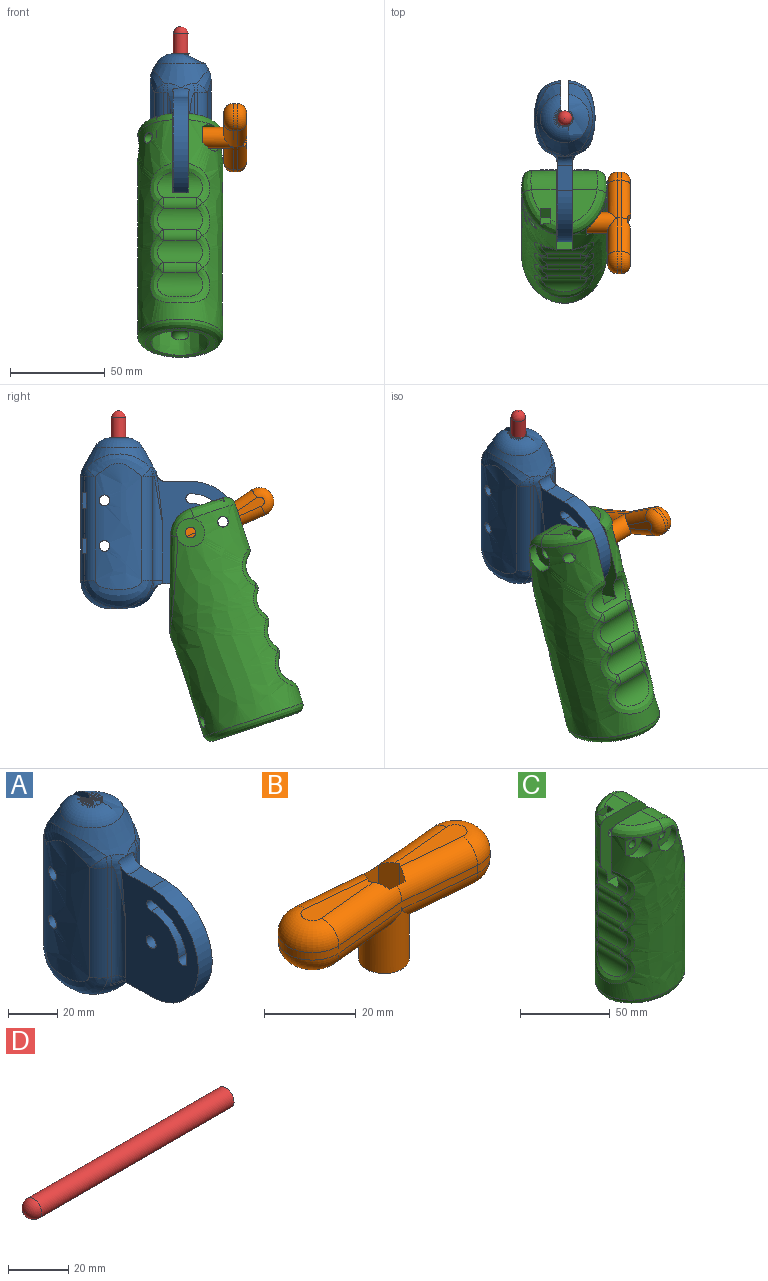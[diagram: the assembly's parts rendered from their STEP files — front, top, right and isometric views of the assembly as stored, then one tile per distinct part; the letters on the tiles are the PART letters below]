
ASSEMBLY  parts=4 mates=3
PART A: 87 faces, bbox 43.8x89x93.8 mm
  f0: cylinder r=20mm len=54.41mm, axis (0,0,-1), area 109.3mm2, adj f43,f48,f56,f66
  f1: cylinder r=20mm len=54.41mm, axis (0,0,-1), area 347.3mm2, adj f12,f14,f15,f17,f28,f29,f31,f43
  f2: torus R=10mm, axis (0,0,1), area 36.3mm2, adj f4,f13,f54,f65
  f3: torus R=10mm, axis (0,0,1), area 10mm2, adj f7,f54,f58,f74
  f4: cylinder r=20mm len=54.41mm, axis (0,0,-1), area 401.1mm2, adj f2,f13,f43,f67
  f5: plane 60.7x48.7mm, normal (1,0,0), area 1782mm2, adj f35,f36,f37,f38,f39,f40,f41,f42
  f6: plane 60.7x48.7mm, normal (-1,0,0), area 1782mm2, adj f35,f36,f37,f38,f39,f40,f41,f42
  f7: cylinder r=20mm len=54.41mm, axis (0,0,-1), area 109.3mm2, adj f3,f43,f44,f72
  f8: cylinder r=2.85mm len=5.7mm, axis (1,0,0), area 85.6mm2, adj f16,f61
  f9: cylinder r=3.95mm len=89.49mm, axis (0,0,-1), area 1833.2mm2, adj f12,f13,f26,f60,f83,f84,f85
  f10: cylinder r=2.85mm len=6mm, axis (1,0,0), area 107.4mm2, adj f13,f23
  f11: cylinder r=2.85mm len=5.7mm, axis (1,0,0), area 71.6mm2, adj f12,f17
  f12: plane 91.73x18.22mm, normal (1,0,0), area 1287.5mm2, adj f1,f9,f11,f26,f27,f43,f54,f57
  f13: plane 91.72x18.22mm, normal (-1,0,0), area 1287.5mm2, adj f2,f4,f9,f10,f25,f26,f43,f54
  f14: plane 14.05x4.5mm, normal (0,0,1), area 59mm2, adj f1,f16,f17,f19,f69
  f15: plane 14.05x4.5mm, normal (0,0,-1), area 59mm2, adj f1,f16,f17,f18,f69
  f16: plane 14.27x8.2mm, normal (1,0,0), area 81.8mm2, adj f8,f14,f15,f18,f19,f69
  f17: plane 16.41x8.2mm, normal (-1,0,0), area 99.4mm2, adj f1,f11,f14,f15,f18,f19
  f18: plane 4.5x4.1mm, normal (0,0.87,-0.5), area 21.3mm2, adj f15,f16,f17,f19
  f19: plane 4.5x4.1mm, normal (0,0.87,0.5), area 21.3mm2, adj f14,f16,f17,f18
  f20: plane 6x5.75mm, normal (0,0,-1), area 31.4mm2, adj f52,f53,f62,f79
  f21: plane 38x2.14mm, normal (0,-1,0), area 81.1mm2, adj f51,f53,f67,f82
  f22: plane 38x6mm, normal (0,1,0), area 227.8mm2, adj f50,f52,f62,f75
  f23: plane 44x12mm, normal (1,0,0), area 469.2mm2, adj f10,f25,f75,f76,f77,f78,f79,f80
  f24: cylinder r=2.85mm len=5.7mm, axis (1,0,0), area 85.6mm2, adj f30,f61
  f25: cylinder r=2.85mm len=6mm, axis (1,0,0), area 107.4mm2, adj f13,f23
  f26: plane 10x9.58mm, normal (0,0,-1), area 42.5mm2, adj f9,f12,f13,f43,f83,f84,f86
  f27: cylinder r=2.85mm len=5.7mm, axis (1,0,0), area 71.6mm2, adj f12,f31
  f28: plane 14.05x4.5mm, normal (0,0,-1), area 59mm2, adj f1,f30,f31,f33,f69
  f29: plane 14.05x4.5mm, normal (0,0,1), area 59mm2, adj f1,f30,f31,f32,f69
  f30: plane 14.27x8.2mm, normal (1,0,0), area 81.8mm2, adj f24,f28,f29,f32,f33,f69
  f31: plane 16.41x8.2mm, normal (-1,0,0), area 99.4mm2, adj f1,f27,f28,f29,f32,f33
  f32: plane 4.5x4.1mm, normal (0,0.87,0.5), area 21.3mm2, adj f29,f30,f31,f33
  f33: plane 4.5x4.1mm, normal (0,0.87,-0.5), area 21.3mm2, adj f28,f30,f31,f32
  f34: plane 6x5.75mm, normal (0,0,1), area 31.4mm2, adj f50,f51,f62,f78
  f35: plane 13.32x8mm, normal (0,0,1), area 104.9mm2, adj f5,f6,f37,f46
  f36: plane 14.6x8mm, normal (0,0,-1), area 115mm2, adj f5,f6,f37,f47
  f37: cylinder r=27mm len=54mm, axis (-1,0,0), area 678.6mm2, adj f5,f6,f35,f36
  f38: cylinder r=2.85mm len=8mm, axis (1,0,0), area 143.3mm2, adj f5,f6
  f39: cylinder r=15.5mm len=15.5mm, axis (1,0,0), area 194.8mm2, adj f5,f6,f40,f42
  f40: cylinder r=2.5mm len=8mm, axis (1,0,0), area 62.8mm2, adj f5,f6,f39,f41
  f41: cylinder r=20.5mm len=20.5mm, axis (1,0,0), area 257.6mm2, adj f5,f6,f40,f42
  f42: cylinder r=2.5mm len=8mm, axis (1,0,0), area 62.8mm2, adj f5,f6,f39,f41
  f43: torus R=5mm, axis (0,0,-1), area 773.6mm2, adj f0,f1,f4,f7,f12,f13,f26,f45
  f44: cylinder r=5mm len=54.41mm, axis (0,0,-1), area 250.9mm2, adj f6,f7,f45,f58
  f45: bspline ~10.07x6.08mm, area 23mm2, adj f6,f43,f44,f47
  f46: torus R=25mm, axis (0,0,-1), area 62.4mm2, adj f5,f6,f35,f54,f55,f58
  f47: torus R=23.73mm, axis (0,0,-1), area 62.5mm2, adj f5,f6,f36,f43,f45,f49
  f48: cylinder r=5mm len=54.41mm, axis (0,0,-1), area 250.9mm2, adj f0,f5,f49,f55
  f49: bspline ~10.07x6.08mm, area 23mm2, adj f5,f43,f47,f48
  f50: cylinder r=5mm len=6mm, axis (-1,0,0), area 46.1mm2, adj f22,f34,f62,f76
  f51: cylinder r=5mm len=5mm, axis (1,0,0), area 26.2mm2, adj f21,f34,f62,f67,f80
  f52: cylinder r=5mm len=6mm, axis (-1,0,0), area 46.1mm2, adj f20,f22,f62,f77
  f53: cylinder r=5mm len=5mm, axis (1,0,0), area 26.2mm2, adj f20,f21,f62,f67,f81
  f54: cone r=10mm half-angle=29.1deg, axis (0,0,-1), area 726.9mm2, adj f2,f3,f12,f13,f46,f55,f56,f57
  f55: bspline ~35.83x19.57mm, area 87.3mm2, adj f5,f46,f48,f54,f56
  f56: torus R=10mm, axis (0,0,1), area 10mm2, adj f0,f54,f55,f64
  f57: torus R=10mm, axis (0,0,1), area 36.3mm2, adj f1,f12,f54,f71
  f58: bspline ~35.83x19.57mm, area 87.3mm2, adj f3,f6,f44,f46,f54
  f59: torus R=4.12mm, axis (0,0,1), area 535.2mm2, adj f12,f13,f54,f60
  f60: cone r=3.95mm half-angle=46deg, axis (0,0,1), area 16mm2, adj f9,f12,f13,f59
  f61: extruded ~66.51x24.67mm, area 1528.6mm2, adj f8,f24,f69,f70,f72,f73
  f62: extruded ~66.51x24.67mm, area 960.1mm2, adj f20,f22,f34,f50,f51,f52,f53,f63
  f63: bspline ~35.46x13.76mm, area 236.7mm2, adj f54,f62,f64,f65
  f64: sphere r=10mm, area 21.4mm2, adj f56,f63,f66
  f65: sphere r=10mm, area 21.4mm2, adj f2,f63,f67
  f66: cylinder r=10mm len=54.41mm, axis (0,0,-1), area 410.2mm2, adj f0,f62,f64,f68
  f67: cylinder r=10mm len=54.41mm, axis (0,0,-1), area 251.4mm2, adj f4,f21,f51,f53,f62,f65,f68
  f68: bspline ~35.69x17.25mm, area 434mm2, adj f43,f62,f66,f67
  f69: cylinder r=10mm len=54.41mm, axis (0,0,-1), area 381.9mm2, adj f1,f14,f15,f16,f28,f29,f30,f61
  f70: bspline ~35.69x17.25mm, area 434mm2, adj f43,f61,f69,f72
  f71: sphere r=10mm, area 21.4mm2, adj f57,f69,f73
  f72: cylinder r=10mm len=54.41mm, axis (0,0,-1), area 410.2mm2, adj f7,f61,f70,f74
  f73: bspline ~36.64x13.76mm, area 236.7mm2, adj f54,f61,f71,f74
  f74: sphere r=10mm, area 21.4mm2, adj f3,f72,f73
  f75: cylinder r=2mm len=38mm, axis (0,0,-1), area 119.4mm2, adj f22,f23,f76,f77
  f76: torus R=3mm, axis (-1,0,0), area 21.1mm2, adj f23,f50,f75,f78
  f77: torus R=3mm, axis (-1,0,0), area 21.1mm2, adj f23,f52,f75,f79
  f78: cylinder r=2mm len=6mm, axis (0,-1,0), area 18.8mm2, adj f23,f34,f76,f80
  f79: cylinder r=2mm len=6mm, axis (0,-1,0), area 18.8mm2, adj f20,f23,f77,f81
  f80: torus R=3mm, axis (-1,0,0), area 21.1mm2, adj f23,f51,f78,f82
  f81: torus R=3mm, axis (-1,0,0), area 21.1mm2, adj f23,f53,f79,f82
  f82: cylinder r=2mm len=38mm, axis (0,0,1), area 119.4mm2, adj f21,f23,f80,f81
  f83: plane 3x2.41mm, normal (1,0,0), area 7.2mm2, adj f9,f26,f85,f86
  f84: plane 3x2.41mm, normal (-1,0,0), area 7.2mm2, adj f9,f26,f85,f86
  f85: plane 4.95x4mm, normal (0,0,1), area 17.4mm2, adj f9,f83,f84,f86
  f86: cylinder r=2mm len=4mm, axis (0,0,-1), area 18.8mm2, adj f26,f83,f84,f85
PART B: 32 faces, bbox 59.1x15.1x23.1 mm
  f0: plane 20.27x5mm, normal (0,0,1), area 69.4mm2, adj f4,f6,f21,f25,f26
  f1: cylinder r=2.75mm len=15mm, axis (0,0,-1), area 259.2mm2, adj f8,f31
  f2: plane 20.27x5mm, normal (0,0,1), area 69.4mm2, adj f3,f5,f20,f28,f29
  f3: cylinder r=5mm len=21.9mm, axis (1,0.09,0), area 156.8mm2, adj f2,f4,f15,f20,f29,f30
  f4: cylinder r=5mm len=21.9mm, axis (1,-0.09,0), area 156.8mm2, adj f0,f3,f16,f21,f25,f30
  f5: cylinder r=5mm len=21.9mm, axis (-1,0.09,0), area 156.8mm2, adj f2,f6,f13,f20,f27,f28
  f6: cylinder r=5mm len=21.9mm, axis (-1,-0.09,0), area 156.8mm2, adj f0,f5,f12,f21,f26,f27
  f7: cylinder r=5.5mm len=16mm, axis (0,0,-1), area 431.4mm2, adj f8,f9,f10,f17,f19,f22,f24
  f8: plane 11x11mm, normal (0,0,-1), area 71.3mm2, adj f1,f7
  f9: plane 19.09x5mm, normal (0,0,-1), area 67.6mm2, adj f7,f17,f18,f19
  f10: plane 19.09x5mm, normal (0,0,-1), area 67.6mm2, adj f7,f22,f23,f24
  f11: cylinder r=7.5mm len=15mm, axis (0,0,-1), area 49.9mm2, adj f12,f16,f18,f21
  f12: plane 21.31x2mm, normal (0.09,-1,0), area 42.8mm2, adj f6,f11,f13,f19
  f13: plane 21.31x2mm, normal (-0.09,-1,0), area 42.8mm2, adj f5,f12,f14,f24
  f14: cylinder r=7.5mm len=15mm, axis (0,0,-1), area 49.9mm2, adj f13,f15,f20,f23
  f15: plane 21.31x2mm, normal (-0.09,1,0), area 42.8mm2, adj f3,f14,f16,f22
  f16: plane 21.31x2mm, normal (0.09,1,0), area 42.8mm2, adj f4,f11,f15,f17
  f17: cylinder r=5mm len=21.77mm, axis (-1,0.09,0), area 144.9mm2, adj f7,f9,f16,f18
  f18: torus R=2.5mm, axis (0,0,1), area 148.4mm2, adj f9,f11,f17,f19
  f19: cylinder r=5mm len=21.77mm, axis (1,0.09,0), area 144.9mm2, adj f7,f9,f12,f18
  f20: torus R=2.5mm, axis (0,0,1), area 148.4mm2, adj f2,f3,f5,f14
  f21: torus R=2.5mm, axis (0,0,1), area 148.4mm2, adj f0,f4,f6,f11
  f22: cylinder r=5mm len=21.77mm, axis (-1,-0.09,0), area 144.9mm2, adj f7,f10,f15,f23
  f23: torus R=2.5mm, axis (0,0,1), area 148.4mm2, adj f10,f14,f22,f24
  f24: cylinder r=5mm len=21.77mm, axis (1,-0.09,0), area 144.9mm2, adj f7,f10,f13,f23
  f25: plane 8.12x4.22mm, normal (0.87,-0.5,0), area 36.3mm2, adj f0,f4,f26,f30,f31
  f26: plane 8.12x4.22mm, normal (0.87,0.5,0), area 36.3mm2, adj f0,f6,f25,f27,f31
  f27: plane 6.71x4.77mm, normal (0,1,0), area 31.1mm2, adj f5,f6,f26,f28,f31
  f28: plane 8.12x4.22mm, normal (-0.87,0.5,0), area 36.3mm2, adj f2,f5,f27,f29,f31
  f29: plane 8.12x4.22mm, normal (-0.87,-0.5,0), area 36.3mm2, adj f2,f3,f28,f30,f31
  f30: plane 6.71x4.77mm, normal (0,-1,0), area 31.1mm2, adj f3,f4,f25,f29,f31
  f31: plane 9.47x8.2mm, normal (0,0,1), area 34.5mm2, adj f1,f25,f26,f27,f28,f29,f30
PART C: 55 faces, bbox 56x46x120.9 mm
  f0: plane 47.01x37.01mm, normal (0,0,-1), area 368.9mm2, adj f23,f33
  f1: cylinder r=2.8mm len=7.8mm, axis (0,-1,0), area 137.2mm2, adj f9,f22
  f2: extruded ~111x54.98mm, area 11755.2mm2, adj f8,f9,f11,f17,f19,f21,f22,f28
  f3: cylinder r=2.8mm len=12.8mm, axis (0,-1,0), area 225.2mm2, adj f8,f20
  f4: cylinder r=2.8mm len=12.8mm, axis (0,-1,0), area 225.2mm2, adj f9,f18
  f5: plane 18.19x13.07mm, normal (0,0,1), area 143.4mm2, adj f8,f12,f13,f14,f27,f28
  f6: cylinder r=2.8mm len=5.6mm, axis (0,-1,0), area 52.8mm2, adj f8,f13
  f7: plane 18.19x13.07mm, normal (0,0,1), area 166.9mm2, adj f9,f26,f31
  f8: plane 50.09x44.78mm, normal (0,-1,0), area 1705.4mm2, adj f2,f3,f5,f6,f10,f25,f27,f28
  f9: plane 50.09x44.78mm, normal (0,1,0), area 1705.4mm2, adj f1,f2,f4,f7,f10,f25,f26,f31
  f10: plane 44.25x8.4mm, normal (0,0,1), area 371.7mm2, adj f8,f9,f25,f37
  f11: cylinder r=2.8mm len=6.55mm, axis (0,-1,0), area 82.2mm2, adj f2,f12
  f12: plane 16.92x9.22mm, normal (0,-1,0), area 104.2mm2, adj f5,f11,f14,f15,f16,f28
  f13: plane 16.05x8.35mm, normal (0,1,0), area 108.1mm2, adj f5,f6,f14,f15,f16,f28
  f14: plane 16x5mm, normal (-1,0,0), area 80mm2, adj f5,f12,f13,f16
  f15: plane 16.53x5.74mm, normal (1,0,0), area 75.1mm2, adj f12,f13,f16,f28
  f16: plane 8.3x5mm, normal (0,0,1), area 41.5mm2, adj f12,f13,f14,f15
  f17: cylinder r=7.5mm len=15mm, axis (0,-1,0), area 244.8mm2, adj f2,f18,f30,f32
  f18: plane 15x15mm, normal (0,-1,0), area 152.1mm2, adj f4,f17
  f19: cylinder r=7.5mm len=15mm, axis (0,1,0), area 235.6mm2, adj f2,f20,f29,f30
  f20: plane 15x15mm, normal (0,1,0), area 152.1mm2, adj f3,f19
  f21: cylinder r=7mm len=14mm, axis (0,-1,0), area 194.7mm2, adj f2,f22
  f22: plane 14x12.26mm, normal (0,-1,0), area 118.3mm2, adj f1,f2,f21
  f23: extruded ~70x41mm, area 7900.4mm2, adj f0,f24,f54
  f24: plane 41x31mm, normal (0,0,-1), area 995.4mm2, adj f23
  f25: plane 48.13x33.82mm, normal (0.94,0,0.33), area 970mm2, adj f8,f9,f10,f26,f27,f30
  f26: cylinder r=15mm len=14.17mm, axis (0,1,0), area 239mm2, adj f7,f9,f25,f32
  f27: cylinder r=15mm len=14.17mm, axis (0,1,0), area 239mm2, adj f5,f8,f25,f29
  f28: bspline ~26.81x20.93mm, area 196.6mm2, adj f2,f5,f8,f12,f13,f15,f29
  f29: bspline ~17.17x12.8mm, area 111.3mm2, adj f2,f19,f27,f28,f30
  f30: bspline ~58.22x44.69mm, area 545.1mm2, adj f2,f17,f19,f25,f29,f32
  f31: bspline ~26.81x20.93mm, area 219.4mm2, adj f2,f7,f9,f32
  f32: bspline ~17.17x12.81mm, area 111.3mm2, adj f2,f17,f26,f30,f31
  f33: bspline ~55.03x45.01mm, area 932.1mm2, adj f0,f2
  f34: cylinder r=10mm len=23.72mm, axis (0,-1,0), area 314.3mm2, adj f40,f41
  f35: cylinder r=10mm len=17.37mm, axis (0,-1,0), area 223.6mm2, adj f39,f40,f47,f48
  f36: cylinder r=10mm len=17.37mm, axis (0,-1,0), area 223.6mm2, adj f43,f47,f50,f53
  f37: cylinder r=10mm len=23.72mm, axis (0,-1,0), area 212.4mm2, adj f8,f9,f10,f42,f49,f50
  f38: sphere r=5mm, area 9.9mm2, adj f39,f40,f41
  f39: bspline ~19.23x7.83mm, area 79mm2, adj f2,f35,f38,f44
  f40: cylinder r=5mm len=17.37mm, axis (0,-1,0), area 111.8mm2, adj f34,f35,f38,f45
  f41: bspline ~31.37x21.86mm, area 259.3mm2, adj f2,f34,f38,f45
  f42: bspline ~22.15x13.37mm, area 109.5mm2, adj f2,f9,f37,f46
  f43: bspline ~19.23x7.83mm, area 79mm2, adj f2,f36,f44,f46
  f44: sphere r=5mm, area 9.9mm2, adj f39,f43,f47
  f45: sphere r=5mm, area 9.9mm2, adj f40,f41,f48
  f46: sphere r=5mm, area 9.9mm2, adj f42,f43,f50
  f47: cylinder r=5mm len=17.37mm, axis (0,-1,0), area 111.8mm2, adj f35,f36,f44,f51
  f48: bspline ~19.23x7.83mm, area 79mm2, adj f2,f35,f45,f51
  f49: bspline ~21.25x13.4mm, area 109.5mm2, adj f2,f8,f37,f52
  f50: cylinder r=5mm len=17.37mm, axis (0,-1,0), area 111.8mm2, adj f36,f37,f46,f52
  f51: sphere r=5mm, area 9.9mm2, adj f47,f48,f53
  f52: sphere r=5mm, area 9.9mm2, adj f49,f50,f53
  f53: bspline ~19.23x7.83mm, area 79mm2, adj f2,f36,f51,f52
  f54: torus R=8mm, axis (0,0,1), area 271mm2, adj f2,f23
PART D: 3 faces, bbox 94.4x7.7x7.7 mm
  f0: cylinder r=3.85mm len=90.5mm, axis (-1,0,0), area 2189.2mm2, adj f1,f2
  f1: sphere r=3.85mm, area 93.1mm2, adj f0
  f2: plane 7.7x7.7mm, normal (1,0,0), area 46.6mm2, adj f0
PLACE A t=(-40.49,-57.33,65.19)mm fixed
PLACE B rot(axis=(0.45,0.77,0.45),105.1deg) t=(-28.79,-112.39,65.92)mm
PLACE C rot(axis=(-0.16,0.16,0.97),91.5deg) t=(-40.79,-129.7,-42.2)mm
PLACE D rot(axis=(0.71,0,-0.71),180deg) t=(-40.49,-57.33,120.69)mm
MATE revolute C.f3 <-> A.f37  axis (1,0,0) through (-44.99,-95.33,60.19)mm
MATE revolute A.f0 <-> D.f0  axis (0,0,-1) through (-40.49,-57.33,20.19)mm
MATE revolute C.f1 <-> B.f7  axis (1,0,0) through (-28.79,-112.39,65.92)mm
